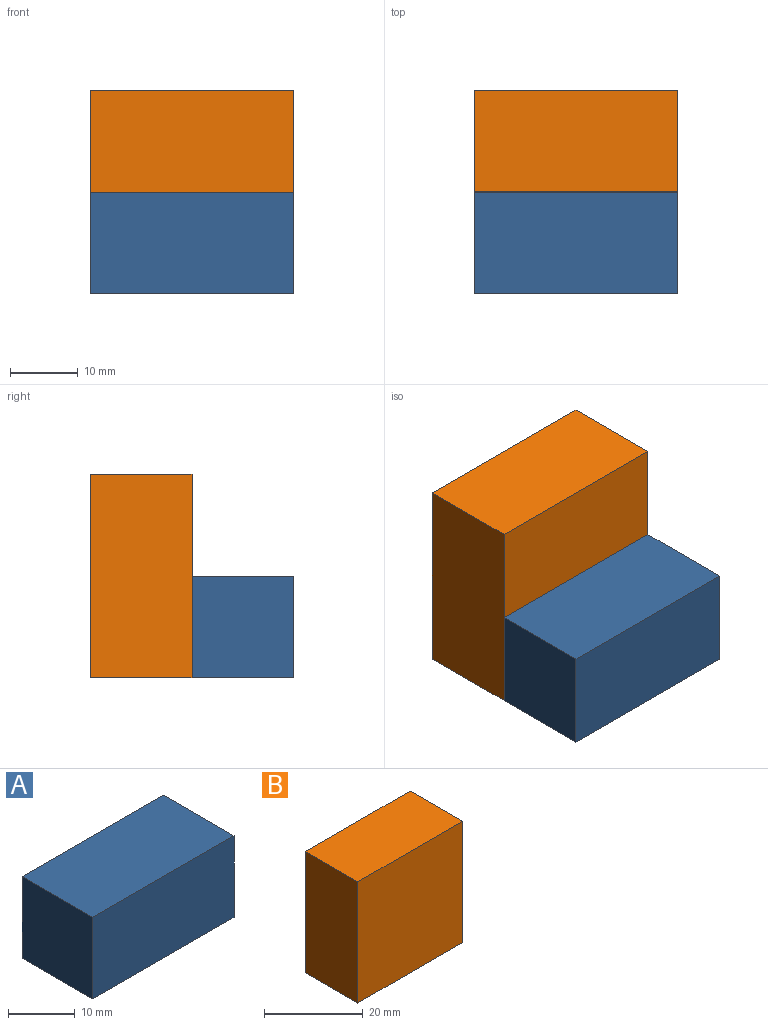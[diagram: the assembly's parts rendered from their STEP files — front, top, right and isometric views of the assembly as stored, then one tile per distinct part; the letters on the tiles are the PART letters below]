
ASSEMBLY  parts=2 mates=1
PART A: 6 faces, bbox 30x15x15 mm
  f0: plane 15x15mm, normal (-1,0,0), area 225mm2, adj f1,f3,f4,f5
  f1: plane 30x15mm, normal (0,0,-1), area 450mm2, adj f0,f2,f4,f5
  f2: plane 15x15mm, normal (1,0,0), area 225mm2, adj f1,f3,f4,f5
  f3: plane 30x15mm, normal (0,0,1), area 450mm2, adj f0,f2,f4,f5
  f4: plane 30x15mm, normal (0,-1,0), area 450mm2, adj f0,f1,f2,f3
  f5: plane 30x15mm, normal (0,1,0), area 450mm2, adj f0,f1,f2,f3
PART B: 6 faces, bbox 30x15x30 mm
  f0: plane 30x15mm, normal (-1,0,0), area 450mm2, adj f1,f3,f4,f5
  f1: plane 30x15mm, normal (0,0,-1), area 450mm2, adj f0,f2,f4,f5
  f2: plane 30x15mm, normal (1,0,0), area 450mm2, adj f1,f3,f4,f5
  f3: plane 30x15mm, normal (0,0,1), area 450mm2, adj f0,f2,f4,f5
  f4: plane 30x30mm, normal (0,-1,0), area 900mm2, adj f0,f1,f2,f3
  f5: plane 30x30mm, normal (0,1,0), area 900mm2, adj f0,f1,f2,f3
PLACE A t=(1.74,10.5,-2.49)mm
PLACE B t=(1.74,25.5,-2.49)mm fixed
MATE fastened A.f5 <-> B.f4  axis (0,1,0) through (16.74,10.5,-2.49)mm
